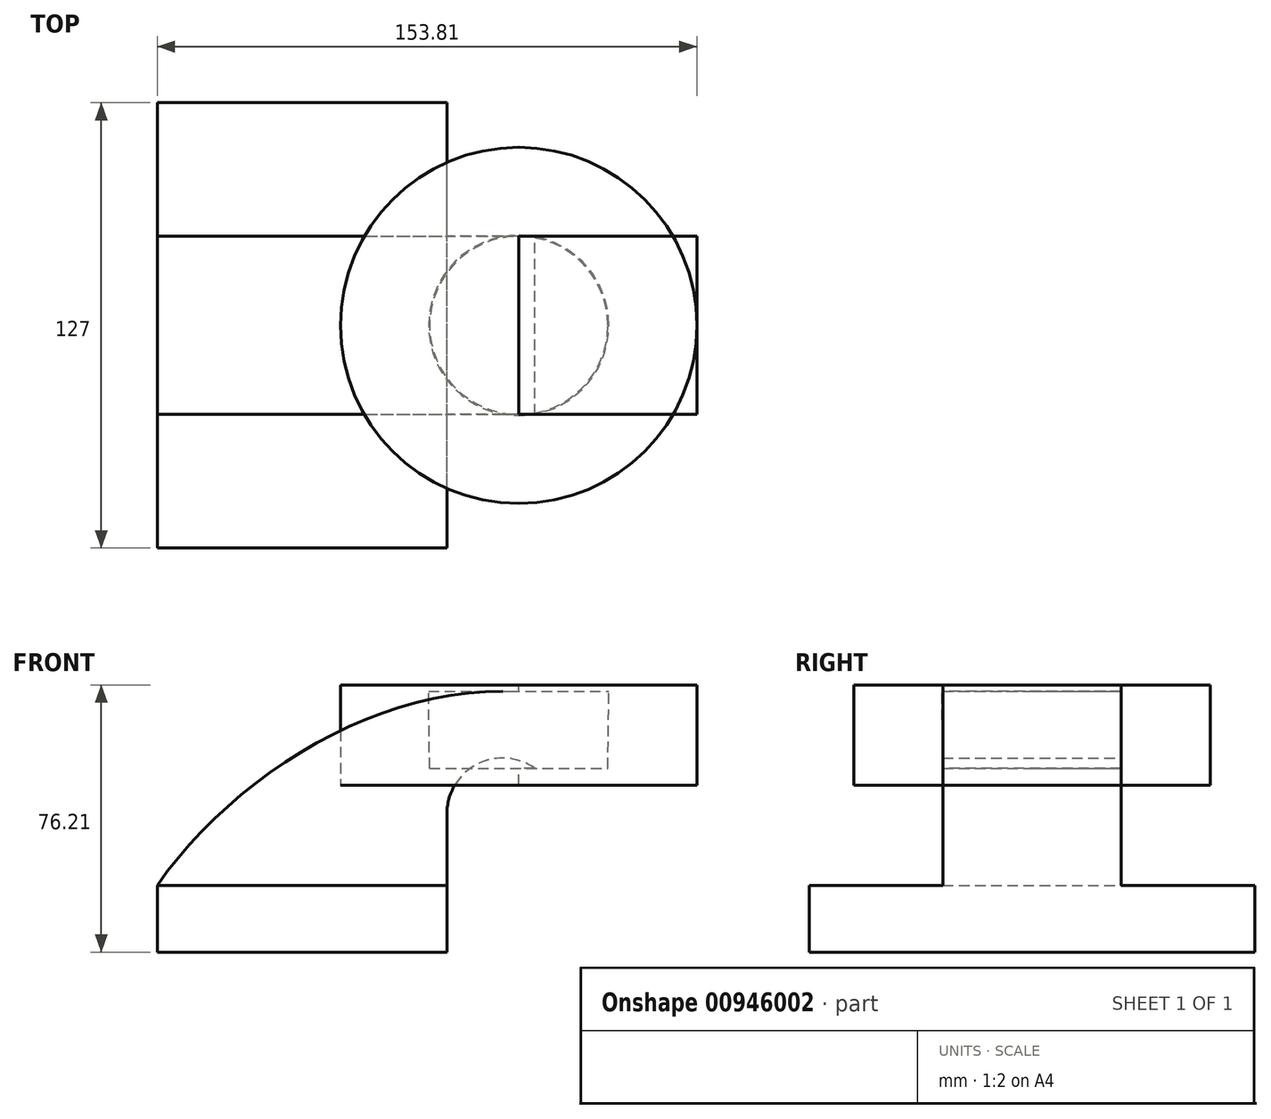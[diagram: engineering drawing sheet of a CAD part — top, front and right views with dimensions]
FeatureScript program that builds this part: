
annotation { "Feature Type Name" : "Feature", "Feature Type Description" : "" }
export const myFeature = defineFeature(function(context is Context, id is Id, definition is map)
    precondition{}
    {
        {
            var Q0;
            Q0=qCreatedBy(makeId("Front.planeOp"),FACE);
            var sketch = newSketch(context, id + "F0", { "sketchPlane" : qUnion([Q0])});
            skLineSegment(sketch, "E0.bottom", {"start": v(-41.28, -9.52) * mm, "end": v(41.28, -9.52) * mm});
            skLineSegment(sketch, "E0.top", {"start": v(-41.28, 9.53) * mm, "end": v(41.28, 9.53) * mm});
            skLineSegment(sketch, "E0.left", {"start": v(-41.28, -9.52) * mm, "end": v(-41.28, 9.53) * mm});
            skLineSegment(sketch, "E0.right", {"start": v(41.28, -9.53) * mm, "end": v(41.28, 9.52) * mm});
            skPoint(sketch, "E0.middle", {"position": v(0, 0) * mm});
            skLineSegment(sketch, "E1.bottom", {"start": v(61.73, 38.1) * mm, "end": v(112.53, 38.1) * mm});
            skLineSegment(sketch, "E1.top", {"start": v(61.73, 66.68) * mm, "end": v(112.53, 66.68) * mm});
            skLineSegment(sketch, "E1.left", {"start": v(61.73, 38.1) * mm, "end": v(61.73, 66.68) * mm});
            skLineSegment(sketch, "E1.right", {"start": v(112.53, 38.1) * mm, "end": v(112.53, 66.68) * mm});
            skPoint(sketch, "E1.middle", {"position": v(87.13, 52.39) * mm});
            skLineSegment(sketch, "E2", {"start": v(41.28, 9.52) * mm, "end": v(41.28, 29.93) * mm});
            skArc(sketch, "E3", {"start": v(41.28, 29.93) * mm, "mid": v(49.86, 44.03) * mm, "end": v(66.34, 42.88) * mm});
            skLineSegment(sketch, "E4", {"start": v(66.34, 42.88) * mm, "end": v(87.13, 42.88) * mm});
            skLineSegment(sketch, "E5", {"start": v(87.13, 42.88) * mm, "end": v(42.68, 42.88) * mm});
            skArc(sketch, "E6.0", {"start": v(22.35, 27.01) * mm, "mid": v(31.44, 53.57) * mm, "end": v(57.15, 64.85) * mm});
            skLineSegment(sketch, "E7.0", {"start": v(22.22, 9.52) * mm, "end": v(22.22, 27) * mm});
            skLineSegment(sketch, "E8", {"start": v(57.15, 64.85) * mm, "end": v(87.42, 64.85) * mm});
            skFitSpline(sketch, "E9", {"points": [v(-41.28, 9.53) * mm, v(57.15, 64.85) * mm], "startDerivative": vector(63.7, 91.87) * mm, "endDerivative": vector(112.1, -0.84) * mm});
            skLineSegment(sketch, "E10", {"start": v(87.42, 64.85) * mm, "end": v(87.13, 42.88) * mm});
            skSolve(sketch);
        }
        {
            var Q0;
            Q0=makeQuery(id+"F0.imprint","IMPRINT",FACE,{"disambiguationData":[TD([[makeQuery(id+"F0.imprint","IMPRINT",EDGE,{"derivedFrom":sQuery(id+"F0.wireOp",EDGE,"E0.bottom")}),1.0]])]});
            extrude(context, id + "F1", {"entities" : qUnion([Q0]), "endBound" : BoundingType.SYMMETRIC, "depth" : 127 * mm, "offsetDistance" : 25.4 * mm});
        }
        {
            var Q0;
            {var subQ5=sQuery(id+"F0.wireOp",EDGE,"E2");Q0=makeQuery(id+"F0.imprint","IMPRINT",FACE,{"disambiguationData":[TD([[makeQuery(id+"F0.imprint","IMPRINT",EDGE,{"derivedFrom":subQ5}),1.0]])]});}
            extrude(context, id + "F2", {"entities" : qUnion([Q0]), "operationType" : NewBodyOperationType.ADD, "endBound" : BoundingType.SYMMETRIC, "depth" : 50.8 * mm, "offsetDistance" : 25.4 * mm});
        }
        {
            var Q0;
            {var subQ1=sQuery(id+"F0.wireOp",EDGE,"E1.bottom");Q0=makeQuery(id+"F0.imprint","IMPRINT",FACE,{"disambiguationData":[TD([[makeQuery(id+"F0.imprint","IMPRINT",EDGE,{"derivedFrom":subQ1}),1.0]])]});}
            var Q1;
            {var subQ1=sQuery(id+"F0.wireOp",EDGE,"E10");Q1=makeQuery(id+"F0.imprint","IMPRINT",FACE,{"disambiguationData":[TD([[makeQuery(id+"F0.imprint","IMPRINT",EDGE,{"derivedFrom":subQ1}),-1.0]])]});}
            extrude(context, id + "F3", {"entities" : qUnion([Q0, Q1]), "operationType" : NewBodyOperationType.ADD, "endBound" : BoundingType.SYMMETRIC, "depth" : 50.8 * mm, "offsetDistance" : 25.4 * mm});
        }
        {
            var Q0;
            {var subQ1=sQuery(id+"F0.wireOp",EDGE,"E1.bottom");Q0=makeQuery(id+"F0.imprint","IMPRINT",FACE,{"disambiguationData":[TD([[makeQuery(id+"F0.imprint","IMPRINT",EDGE,{"derivedFrom":subQ1}),1.0]])]});}
            var Q1;
            Q1=sQuery(id+"F0.wireOp",EDGE,"E1.left");
            revolve(context, id + "F4", {"surfaceOperationType" : NewSurfaceOperationType.NEW, "entities" : qUnion([Q0]), "axis" : qUnion([Q1]), "revolveType" : RevolveType.FULL});
        }
    });
